# Revit family: 4.Кассетный воздушный фильтр для круглых каналов FKS
name_source: partatom
category: Оборудование
revit_build: Autodesk Revit 2016 (Build: 20151209_0715(x64)
units: mm (PartAtom-declared; Revit-internal decimal feet)

## family parameters
Всегда вертикально = Да
На основе рабочей плоскости = Нет
Общий = Нет
При загрузке вырезать с полостями = Нет
Размер круглого соединителя = Использовать диаметр
Тип детали = Нормальный
Точка расчета площади = Нет

## types (6) — shared parameters
Единица измерения = шт.
Завод изготовитель = KORF
Заправочный объем, л = 0.4 м³
Ключевая пометка = Вентиляция
Материал = Сталь серая
Наименование и тех.хар-ка = Кассетный воздушный фильтр для круглых каналов
Раздел = ОВ
отступ = 60 мм

## per-type parameters (varying)
| type | А | Б | Д | Д1 | Масса единицы | Тип, марка, обозначение |
| 100 | 139 мм | 138 мм | 100 мм | 98 мм | 0.8 кг | FKS 100 |
| 125 | 169 мм | 168 мм | 125 мм | 123 мм | 1 кг | FKS 125 |
| 160 | 199 мм | 198 мм | 160 мм | 157 мм | 1.2 кг | FKS 160 |
| 200 | 244 мм | 243 мм | 200 мм | 196 мм | 1.6 кг | FKS 200 |
| 250 | 294 мм | 293 мм | 250 мм | 245 мм | 2 кг | FKS 250 |
| 315 | 359 мм | 358 мм | 315 мм | 309 мм | 2.4 кг | FKS 315 |
